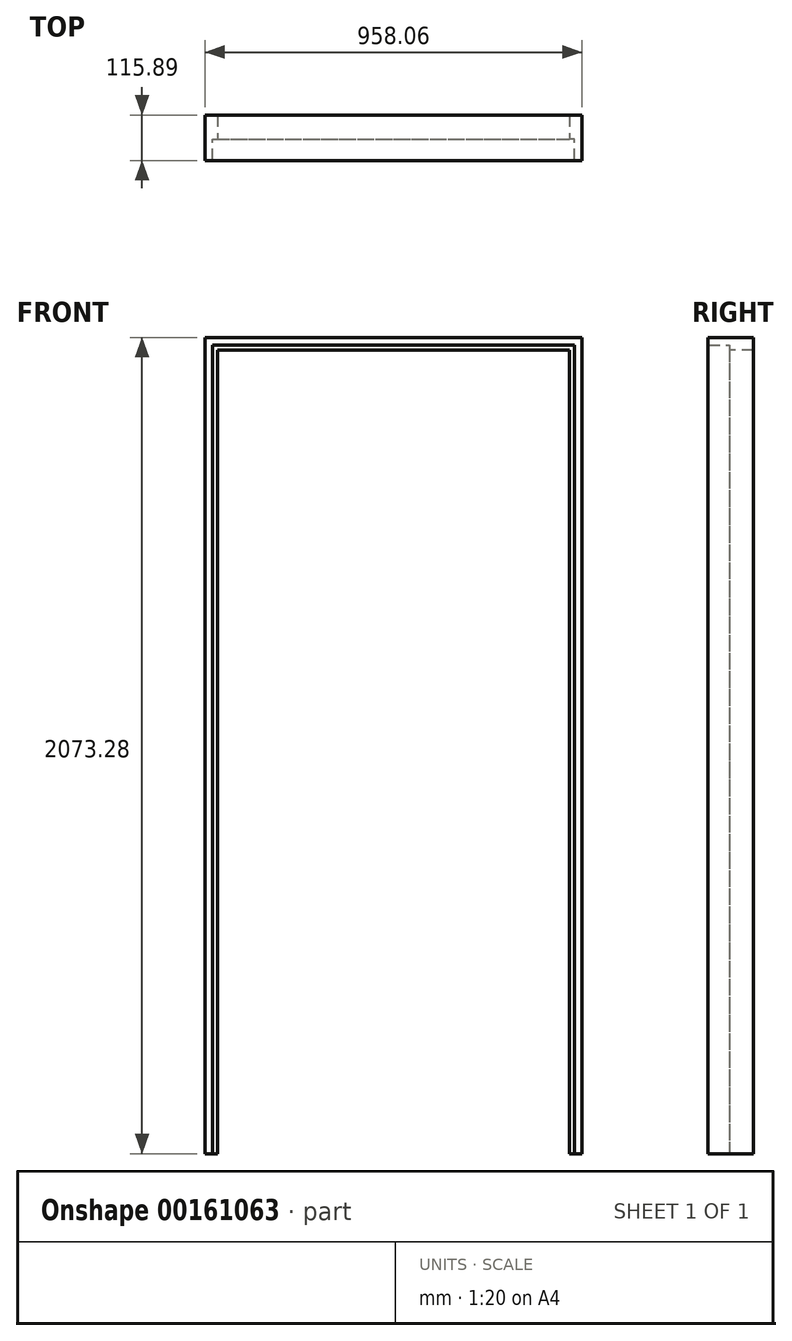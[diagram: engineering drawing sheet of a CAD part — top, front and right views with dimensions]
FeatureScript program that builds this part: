
annotation { "Feature Type Name" : "Feature", "Feature Type Description" : "" }
export const myFeature = defineFeature(function(context is Context, id is Id, definition is map)
    precondition{}
    {
        {
            var Q0;
            Q0=qCreatedBy(makeId("Front.planeOp"),FACE);
            cPlane(context, id + "F0", {"entities" : qUnion([Q0]), "cplaneType" : CPlaneType.OFFSET, "offset" : 3.17 * mm, "oppositeDirection" : true, "width" : 152.4 * mm, "height" : 152.4 * mm});
        }
        {
            var Q0;
            Q0=qCreatedBy(makeId("Front.planeOp"),FACE);
            var sketch = newSketch(context, id + "F1", { "sketchPlane" : qUnion([Q0])});
            skLineSegment(sketch, "E0.bottom", {"start": v(0, 0) * mm, "end": v(19.05, 0) * mm});
            skLineSegment(sketch, "E0.top", {"start": v(0, 2054.23) * mm, "end": v(19.05, 2054.23) * mm});
            skLineSegment(sketch, "E0.left", {"start": v(0, 0) * mm, "end": v(0, 2054.23) * mm});
            skLineSegment(sketch, "E0.right", {"start": v(19.05, 0) * mm, "end": v(19.05, 2054.23) * mm});
            skLineSegment(sketch, "E1.bottom", {"start": v(31.75, 2041.53) * mm, "end": v(19.05, 2041.53) * mm});
            skLineSegment(sketch, "E1.top", {"start": v(31.75, 0) * mm, "end": v(19.05, 0) * mm});
            skLineSegment(sketch, "E1.left", {"start": v(31.75, 2041.53) * mm, "end": v(31.75, 0) * mm});
            skLineSegment(sketch, "E1.right", {"start": v(19.05, 2041.53) * mm, "end": v(19.05, 0) * mm});
            skLineSegment(sketch, "E2.bottom", {"start": v(0, 2054.23) * mm, "end": v(958.06, 2054.23) * mm});
            skLineSegment(sketch, "E2.top", {"start": v(0, 2073.28) * mm, "end": v(958.06, 2073.28) * mm});
            skLineSegment(sketch, "E2.left", {"start": v(0, 2054.23) * mm, "end": v(0, 2073.28) * mm});
            skLineSegment(sketch, "E2.right", {"start": v(958.06, 2054.23) * mm, "end": v(958.06, 2073.28) * mm});
            skPoint(sketch, "E3.oppositeSnap0", {"position": v(9.53, 0) * mm});
            skLineSegment(sketch, "E3.bottom", {"start": v(958.06, 2054.23) * mm, "end": v(939, 2054.23) * mm});
            skLineSegment(sketch, "E3.top", {"start": v(958.06, 0) * mm, "end": v(939, 0) * mm});
            skLineSegment(sketch, "E3.left", {"start": v(958.06, 2054.23) * mm, "end": v(958.06, 0) * mm});
            skLineSegment(sketch, "E3.right", {"start": v(939, 2054.23) * mm, "end": v(939, 0) * mm});
            skLineSegment(sketch, "E4.bottom", {"start": v(939, 0) * mm, "end": v(926.3, 0) * mm});
            skLineSegment(sketch, "E4.top", {"start": v(939, 2041.53) * mm, "end": v(926.3, 2041.53) * mm});
            skLineSegment(sketch, "E4.left", {"start": v(939, 0) * mm, "end": v(939, 2041.53) * mm});
            skLineSegment(sketch, "E4.right", {"start": v(926.3, 0) * mm, "end": v(926.3, 2041.53) * mm});
            skLineSegment(sketch, "E5.bottom", {"start": v(19.05, 2054.23) * mm, "end": v(939, 2054.23) * mm});
            skLineSegment(sketch, "E5.left", {"start": v(19.05, 2054.23) * mm, "end": v(19.05, 2041.53) * mm});
            skLineSegment(sketch, "E5.right", {"start": v(939, 2054.23) * mm, "end": v(939, 2041.53) * mm});
            skLineSegment(sketch, "E6.bottom", {"start": v(19.05, 2054.23) * mm, "end": v(593.72, 2054.23) * mm});
            skLineSegment(sketch, "E7", {"start": v(31.75, 2041.53) * mm, "end": v(926.3, 2041.53) * mm});
            skSolve(sketch);
        }
        {
            var Q0;
            Q0=qCreatedBy(id+"F0.planeOp",FACE);
            var sketch = newSketch(context, id + "F2", { "sketchPlane" : qUnion([Q0])});
            skLineSegment(sketch, "E8.0", {"start": v(0, 0) * mm, "end": v(0, 2054.23) * mm});
            skLineSegment(sketch, "E9.0", {"start": v(0, 0) * mm, "end": v(19.05, 0) * mm});
            skLineSegment(sketch, "E10.0", {"start": v(31.75, 0) * mm, "end": v(19.05, 0) * mm});
            skLineSegment(sketch, "E11.0", {"start": v(31.75, 2041.53) * mm, "end": v(31.75, 0) * mm});
            skLineSegment(sketch, "E12.0", {"start": v(0, 2073.28) * mm, "end": v(958.06, 2073.28) * mm});
            skLineSegment(sketch, "E13.0", {"start": v(0, 2054.23) * mm, "end": v(0, 2073.28) * mm});
            skLineSegment(sketch, "E14.0", {"start": v(926.3, 0) * mm, "end": v(926.3, 2041.53) * mm});
            skLineSegment(sketch, "E15.0", {"start": v(958.06, 2054.23) * mm, "end": v(958.06, 0) * mm});
            skLineSegment(sketch, "E16.0", {"start": v(958.06, 2054.23) * mm, "end": v(958.06, 2073.28) * mm});
            skLineSegment(sketch, "E17.0", {"start": v(939, 0) * mm, "end": v(926.3, 0) * mm});
            skLineSegment(sketch, "E18.0", {"start": v(958.06, 0) * mm, "end": v(939, 0) * mm});
            skLineSegment(sketch, "E19.0", {"start": v(31.75, 2041.53) * mm, "end": v(926.3, 2041.53) * mm});
            skSolve(sketch);
        }
        {
            var Q0;
            Q0=qSketchRegion(id+"F2",true);
            extrude(context, id + "F3", {"entities" : qUnion([Q0]), "oppositeDirection" : true, "depth" : 61.9 * mm});
        }
        {
            var Q0;
            Q0=qCreatedBy(makeId("Front.planeOp"),FACE);
            var sketch = newSketch(context, id + "F4", { "sketchPlane" : qUnion([Q0])});
            skLineSegment(sketch, "E20.0", {"start": v(0, 0) * mm, "end": v(19.05, 0) * mm});
            skLineSegment(sketch, "E21.0", {"start": v(19.05, 2041.53) * mm, "end": v(19.05, 0) * mm});
            skLineSegment(sketch, "E22.0", {"start": v(0, 0) * mm, "end": v(0, 2054.23) * mm});
            skLineSegment(sketch, "E23.0", {"start": v(0, 2054.23) * mm, "end": v(0, 2073.28) * mm});
            skLineSegment(sketch, "E24.0", {"start": v(0, 2073.28) * mm, "end": v(958.06, 2073.28) * mm});
            skLineSegment(sketch, "E25.0", {"start": v(19.05, 2054.23) * mm, "end": v(19.05, 2041.53) * mm});
            skLineSegment(sketch, "E26.0", {"start": v(19.05, 2054.23) * mm, "end": v(593.72, 2054.23) * mm});
            skLineSegment(sketch, "E27.0", {"start": v(939, 2054.23) * mm, "end": v(939, 2041.53) * mm});
            skLineSegment(sketch, "E28.0", {"start": v(939, 0) * mm, "end": v(939, 2041.53) * mm});
            skLineSegment(sketch, "E29.0", {"start": v(958.06, 2054.23) * mm, "end": v(958.06, 0) * mm});
            skPoint(sketch, "E30.0", {"position": v(958.06, 2063.75) * mm});
            skLineSegment(sketch, "E31.0", {"start": v(958.06, 2054.23) * mm, "end": v(958.06, 2073.28) * mm});
            skLineSegment(sketch, "E32", {"start": v(364.33, 2054.23) * mm, "end": v(939, 2054.23) * mm});
            skLineSegment(sketch, "E33.0", {"start": v(958.06, 0) * mm, "end": v(939, 0) * mm});
            skLineSegment(sketch, "E34", {"start": v(593.72, 2054.23) * mm, "end": v(939, 2054.23) * mm});
            skSolve(sketch);
        }
        {
            var Q0;
            Q0=qSketchRegion(id+"F4",true);
            extrude(context, id + "F5", {"entities" : qUnion([Q0]), "operationType" : NewBodyOperationType.ADD, "depth" : 50.8 * mm, "hasSecondDirection" : true, "secondDirectionOppositeDirection" : true, "secondDirectionDepth" : 3.17 * mm});
        }
    });
